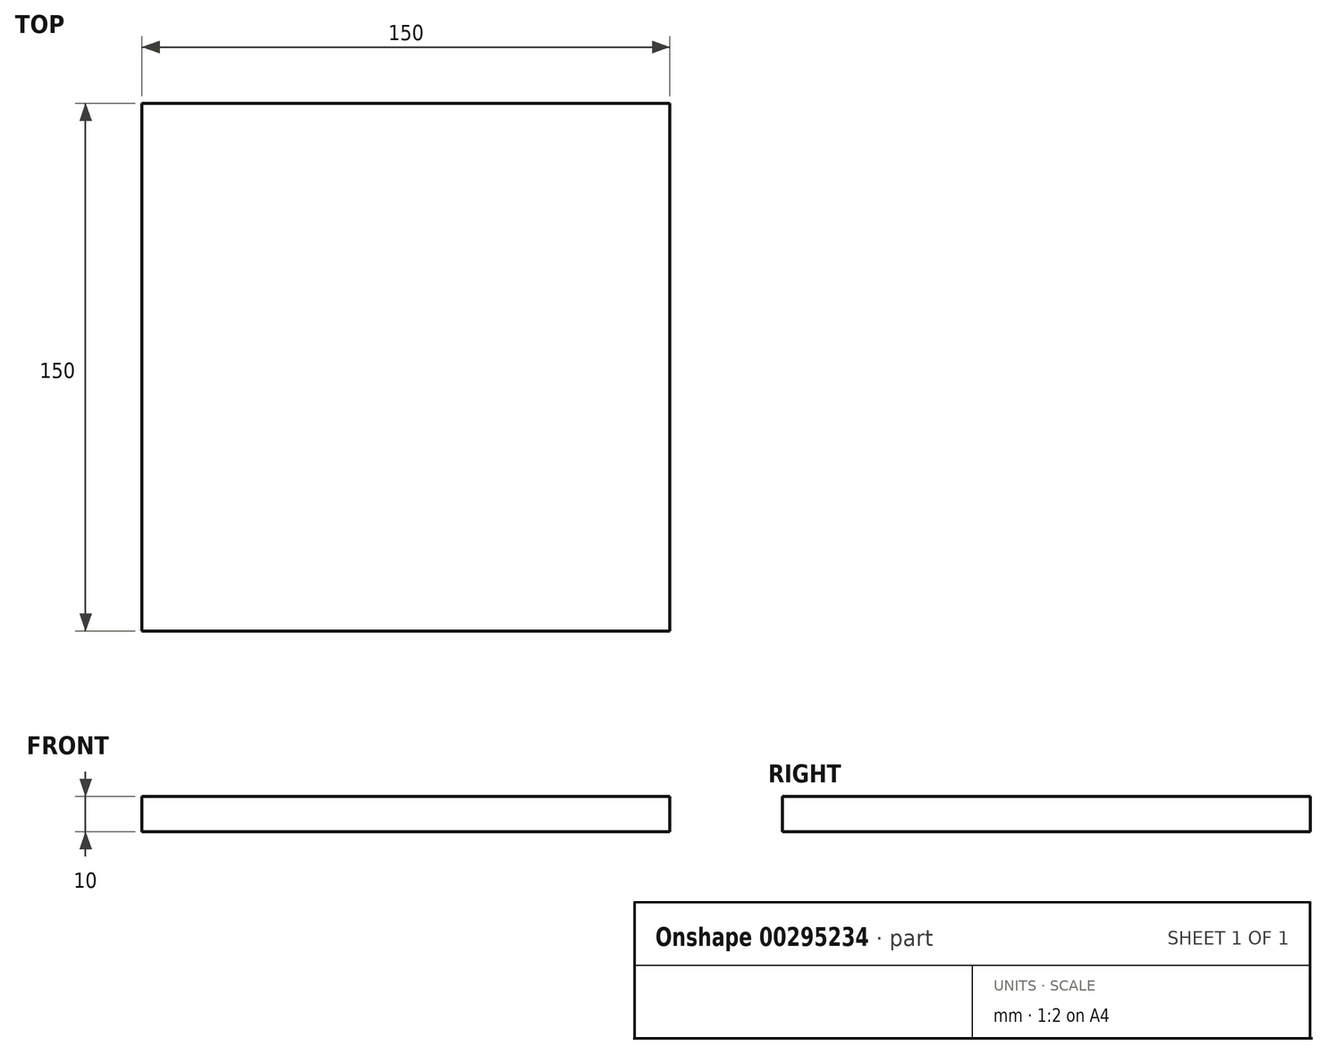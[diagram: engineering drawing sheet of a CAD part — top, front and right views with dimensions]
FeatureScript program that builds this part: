
annotation { "Feature Type Name" : "Feature", "Feature Type Description" : "" }
export const myFeature = defineFeature(function(context is Context, id is Id, definition is map)
    precondition{}
    {
        {
            var Q0;
            Q0=qCreatedBy(makeId("Top.planeOp"),FACE);
            var sketch = newSketch(context, id + "F0", { "sketchPlane" : qUnion([Q0])});
            skLineSegment(sketch, "E0.bottom", {"start": v(75, -75) * mm, "end": v(-75, -75) * mm});
            skLineSegment(sketch, "E0.top", {"start": v(75, 75) * mm, "end": v(-75, 75) * mm});
            skLineSegment(sketch, "E0.left", {"start": v(75, -75) * mm, "end": v(75, 75) * mm});
            skLineSegment(sketch, "E0.right", {"start": v(-75, -75) * mm, "end": v(-75, 75) * mm});
            skPoint(sketch, "E0.middle", {"position": v(0, 0) * mm});
            skSolve(sketch);
        }
        {
            var Q0;
            Q0 = qSketchRegion(id + "F0", true);
            extrude(context, id + "F1", {"entities" : qUnion([Q0]), "depth" : 10 * mm});
        }
    });
